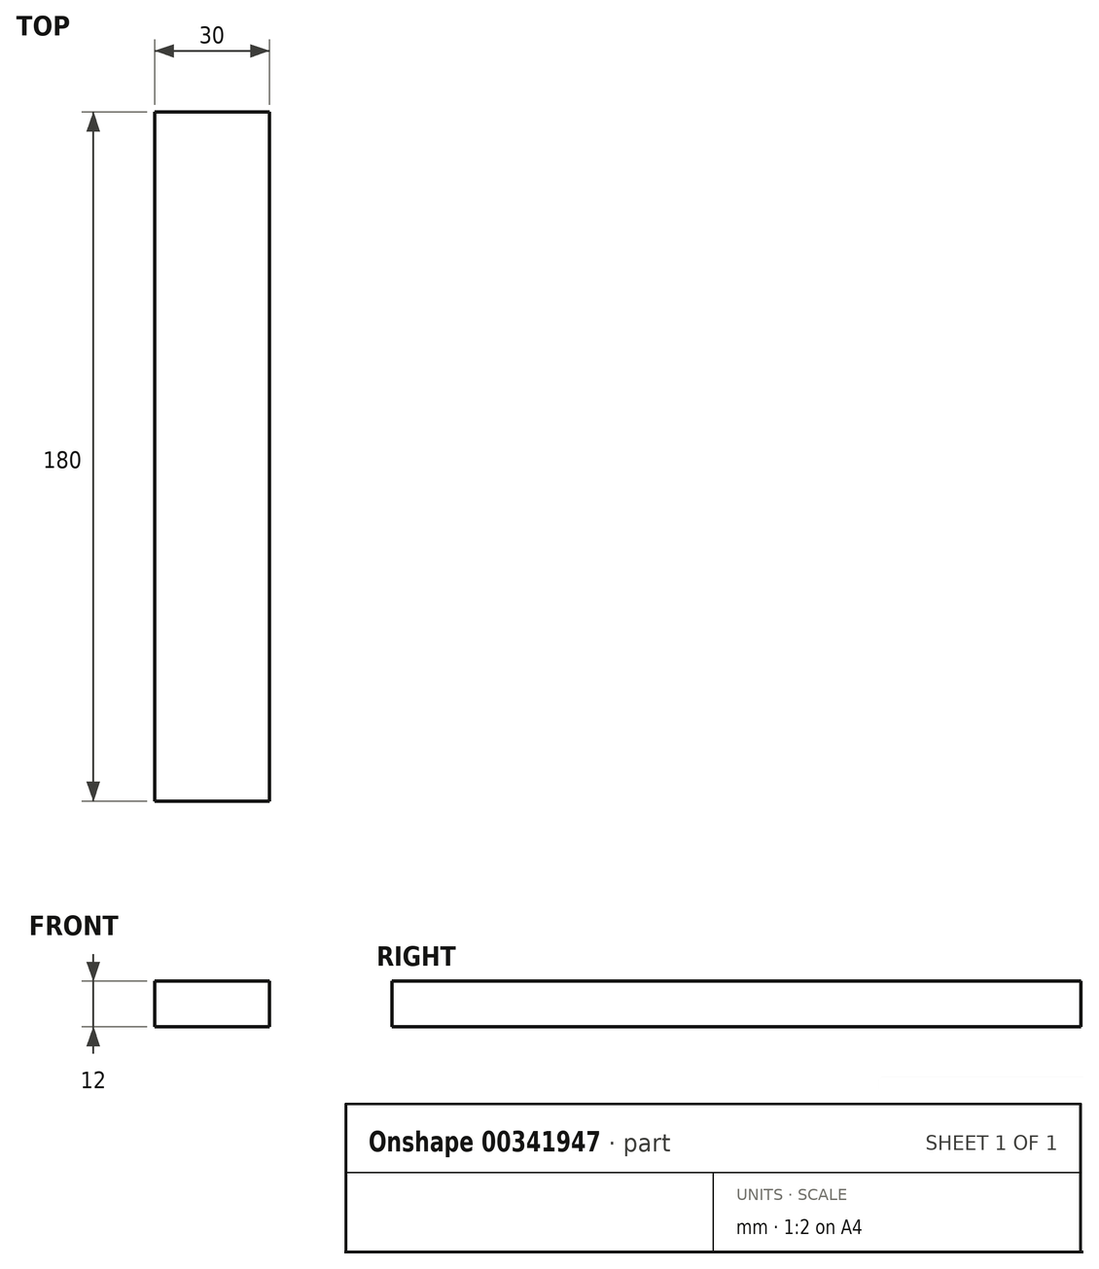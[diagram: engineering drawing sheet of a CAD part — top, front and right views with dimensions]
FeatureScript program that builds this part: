
annotation { "Feature Type Name" : "Feature", "Feature Type Description" : "" }
export const myFeature = defineFeature(function(context is Context, id is Id, definition is map)
    precondition{}
    {
        {
            var Q0;
            Q0=qCreatedBy(makeId("Front.planeOp"),FACE);
            var sketch = newSketch(context, id + "F0", { "sketchPlane" : qUnion([Q0])});
            skLineSegment(sketch, "E0.bottom", {"start": v(15, -6) * mm, "end": v(-15, -6) * mm});
            skLineSegment(sketch, "E0.top", {"start": v(15, 6) * mm, "end": v(-15, 6) * mm});
            skLineSegment(sketch, "E0.left", {"start": v(15, -6) * mm, "end": v(15, 6) * mm});
            skLineSegment(sketch, "E0.right", {"start": v(-15, -6) * mm, "end": v(-15, 6) * mm});
            skPoint(sketch, "E0.middle", {"position": v(0, 0) * mm});
            skSolve(sketch);
        }
        {
            var Q0;
            Q0=makeQuery(id+"F0.imprint","IMPRINT",FACE,{"disambiguationData":[TD([[makeQuery(id+"F0.imprint","IMPRINT",EDGE,{"derivedFrom":sQuery(id+"F0.wireOp",EDGE,"E0.bottom")}),-1.0]])]});
            extrude(context, id + "F1", {"entities" : qUnion([Q0]), "depth" : 90 * mm, "hasSecondDirection" : true, "secondDirectionOppositeDirection" : true, "secondDirectionDepth" : 90 * mm});
        }
    });
